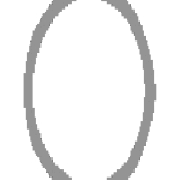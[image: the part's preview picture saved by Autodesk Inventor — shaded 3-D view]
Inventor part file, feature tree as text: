
AUTODESK INVENTOR PART (.ipt)
format: ipt  version: 2021 (Build 250183000, 183)  size: 112,640 bytes
history: native  units: in
note: dims shown in document units (in); Inventor stores cm internally (conversion verified against a paired STEP export)
features: other x4, sketch x3, plane x1
ambient origin geometry x8: Origin, YZ Plane, XZ Plane, XY Plane, X Axis, Y Axis, Z Axis, Center Point
bodies: Solid1 (feature_tree), Body (feature_tree)
feature tree (8):
  other  "Driven Length"
  other  "Frame Generator"
  other  "Start Plane"
  other  "End Plane"
  sketch  "Sketch"  dims[d2=15.2522in d4=-0.0in d5=15.2522in d6=0.12in d7=0.0in d8=90.0deg d9=15.2522in]
  sketch  "Sketch2"  dims[d0=1.0in]
  plane  "Work Plane3"
  sketch  "Sketch3"  dims[d1=0.065in]
